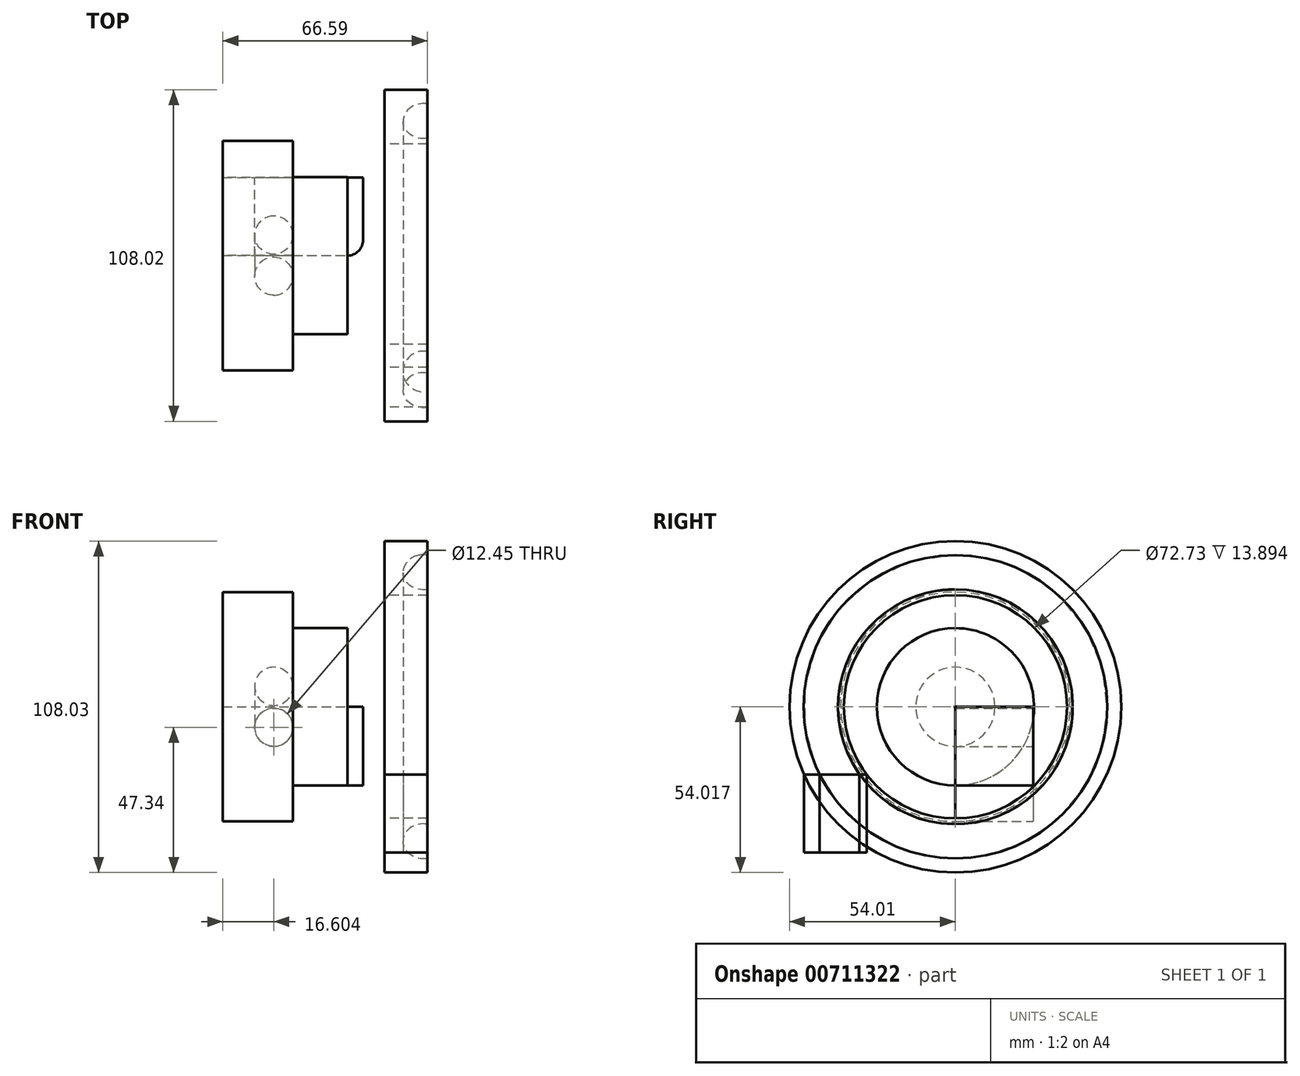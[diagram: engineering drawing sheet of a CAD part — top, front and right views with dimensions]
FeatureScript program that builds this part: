
annotation { "Feature Type Name" : "Feature", "Feature Type Description" : "" }
export const myFeature = defineFeature(function(context is Context, id is Id, definition is map)
    precondition{}
    {
        {
            var Q0;
            Q0=qCreatedBy(makeId("Front.planeOp"),FACE);
            var sketch = newSketch(context, id + "F0", { "sketchPlane" : qUnion([Q0])});
            skLineSegment(sketch, "E0.bottom", {"start": v(9.2, 21.83) * mm, "end": v(54.86, 21.83) * mm});
            skLineSegment(sketch, "E0.top", {"start": v(9.2, 47.46) * mm, "end": v(54.86, 47.46) * mm});
            skLineSegment(sketch, "E0.left", {"start": v(9.2, 21.83) * mm, "end": v(9.2, 47.46) * mm});
            skLineSegment(sketch, "E0.right", {"start": v(54.86, 21.83) * mm, "end": v(54.86, 47.46) * mm});
            skLineSegment(sketch, "E1.bottom", {"start": v(32.03, 21.83) * mm, "end": v(9.2, 21.83) * mm});
            skLineSegment(sketch, "E1.top", {"start": v(32.03, 10.1) * mm, "end": v(9.2, 10.1) * mm});
            skLineSegment(sketch, "E1.left", {"start": v(32.03, 21.83) * mm, "end": v(32.03, 10.1) * mm});
            skLineSegment(sketch, "E1.right", {"start": v(9.2, 21.83) * mm, "end": v(9.2, 10.1) * mm});
            skCircle(sketch, "E2", {"center": v(25.8, 40.78) * mm, "radius": 6.23 * mm});
            skSolve(sketch);
        }
        {
            var Q0;
            Q0 = qSketchRegion(id + "F0", true);
            extrude(context, id + "F1", {"entities" : qUnion([Q0]), "depth" : 25.4 * mm, "offsetDistance" : 25.4 * mm});
        }
        {
            var Q0;
            Q0=qCreatedBy(makeId("Top.planeOp"),FACE);
            var sketch = newSketch(context, id + "F2", { "sketchPlane" : qUnion([Q0])});
            skLineSegment(sketch, "E3.bottom", {"start": v(75.79, -74.7) * mm, "end": v(61.9, -74.7) * mm});
            skLineSegment(sketch, "E3.top", {"start": v(75.79, -54.31) * mm, "end": v(61.9, -54.31) * mm});
            skLineSegment(sketch, "E3.left", {"start": v(75.79, -74.7) * mm, "end": v(75.79, -54.31) * mm});
            skLineSegment(sketch, "E3.right", {"start": v(61.9, -74.7) * mm, "end": v(61.9, -54.31) * mm});
            skCircle(sketch, "E4", {"center": v(74.52, -63.16) * mm, "radius": 6.63 * mm});
            skSolve(sketch);
        }
        {
            var Q0;
            Q0=makeQuery(id+"F1.opExtrude","CAP_EDGE",EDGE,{"disambiguationData":[OSD([sQuery(id+"F0.wireOp",EDGE,"E0.right")])],"isStart":false});
            fillet(context, id + "F3", {"entities" : qUnion([Q0]), "radius" : 5.08 * mm, "tangentPropagation" : true, "allowEdgeOverflow" : false});
        }
        {
            var Q0;
            {var subQ0=sQuery(id+"F2.wireOp",EDGE,"E4");var subQ1=sQuery(id+"F2.wireOp",EDGE,"E3.left");var subQ2=makeQuery(id+"F2.imprint","INTERSECT",VERTEX,{"disambiguationData":[OD(0.0)],"derivedFrom":[subQ1,subQ0]});Q0=makeQuery(id+"F2.imprint","IMPRINT",FACE,{"disambiguationData":[TD([[makeQuery(id+"F2.imprint","IMPRINT",EDGE,{"disambiguationData":[TD([[subQ2,-1.0]])],"derivedFrom":subQ1}),1.0]])]});}
            var Q1;
            {var subQ0=sQuery(id+"F2.wireOp",EDGE,"E4");var subQ1=sQuery(id+"F2.wireOp",EDGE,"E3.left");var subQ2=makeQuery(id+"F2.imprint","INTERSECT",VERTEX,{"disambiguationData":[OD(0.0)],"derivedFrom":[subQ1,subQ0]});Q1=makeQuery(id+"F2.imprint","IMPRINT",FACE,{"disambiguationData":[TD([[makeQuery(id+"F2.imprint","IMPRINT",EDGE,{"disambiguationData":[TD([[subQ2,-1.0]])],"derivedFrom":subQ1}),-1.0]])]});}
            extrude(context, id + "F4", {"entities" : qUnion([Q0, Q1]), "depth" : 25.4 * mm, "offsetDistance" : 25.4 * mm});
        }
        {
            var Q0;
            Q0=makeQuery(id+"F4.opExtrude","CAP_FACE",FACE,{"disambiguationData":[OSD([sQuery(id+"F2.wireOp",EDGE,"E4")])],"isStart":false});
            var Q1;
            Q1=makeQuery(id+"F1.opExtrude","CAP_FACE",FACE,{"disambiguationData":[OSD([sQuery(id+"F0.wireOp",EDGE,"E0.bottom"),sQuery(id+"F0.wireOp",EDGE,"E0.top"),sQuery(id+"F0.wireOp",EDGE,"E0.left"),sQuery(id+"F0.wireOp",EDGE,"E0.right"),sQuery(id+"F0.wireOp",EDGE,"E1.top"),sQuery(id+"F0.wireOp",EDGE,"E1.left"),sQuery(id+"F0.wireOp",EDGE,"E1.right"),sQuery(id+"F0.wireOp",EDGE,"E2")])],"isStart":false});
            var Q2;
            Q2=makeQuery(id+"F1.opExtrude","CAP_EDGE",EDGE,{"disambiguationData":[OSD([sQuery(id+"F0.wireOp",EDGE,"E0.top")])],"isStart":false});
            revolve(context, id + "F5", {"surfaceOperationType" : NewSurfaceOperationType.NEW, "entities" : qUnion([Q0, Q1]), "axis" : qUnion([Q2]), "revolveType" : RevolveType.FULL});
        }
    });
